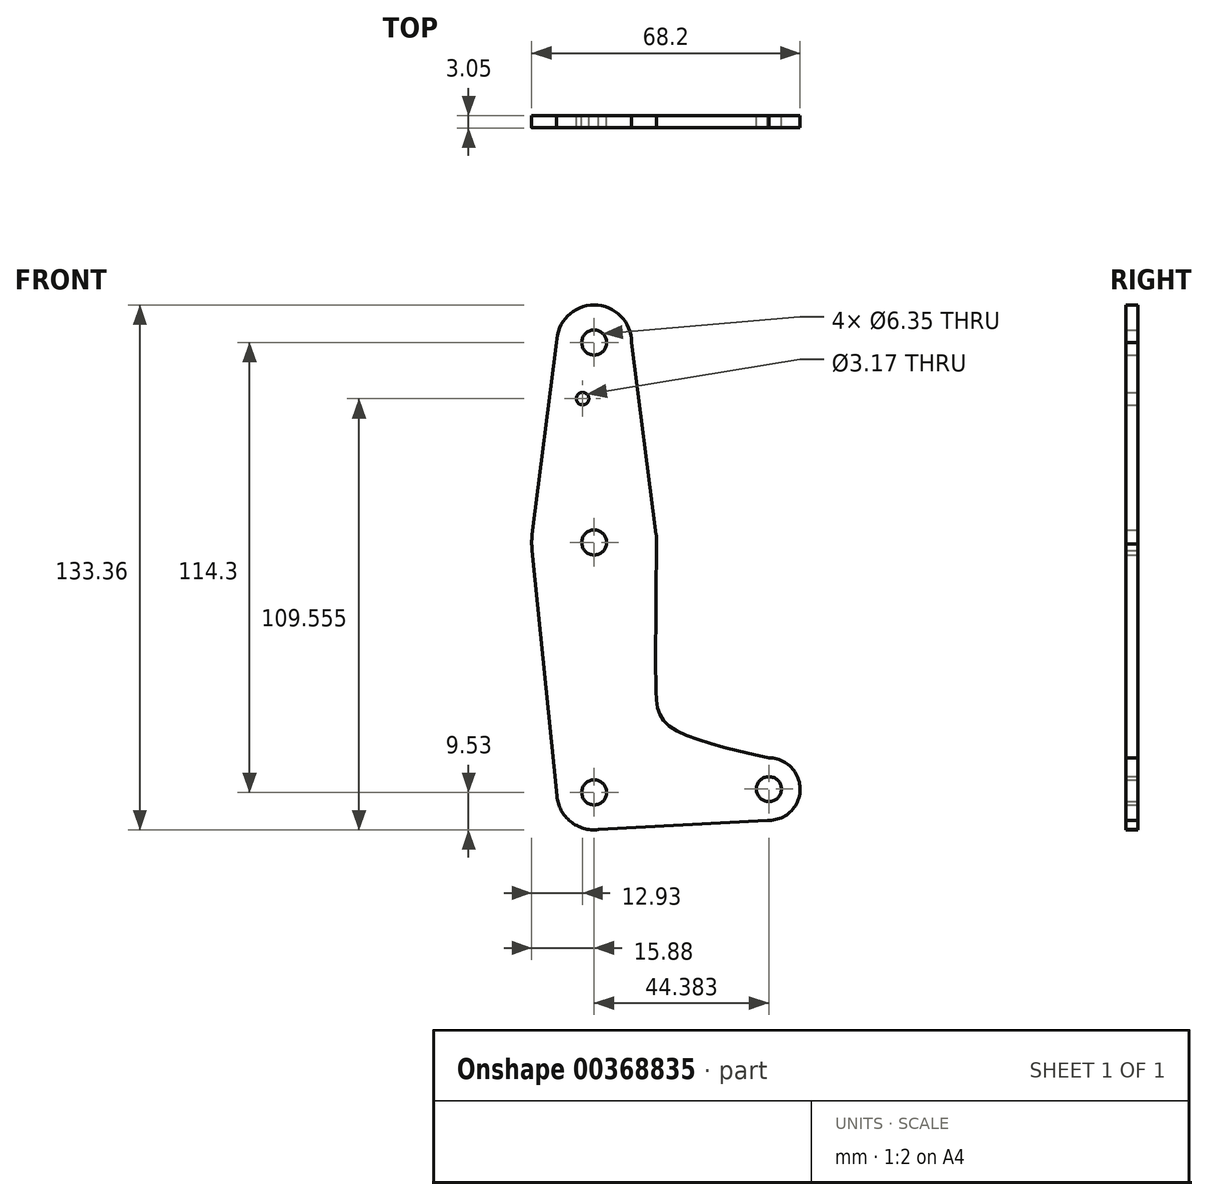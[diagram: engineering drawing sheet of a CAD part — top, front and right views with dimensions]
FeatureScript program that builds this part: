
annotation { "Feature Type Name" : "Feature", "Feature Type Description" : "" }
export const myFeature = defineFeature(function(context is Context, id is Id, definition is map)
    precondition{}
    {
        {
            var Q0;
            Q0=qCreatedBy(makeId("Front.planeOp"),FACE);
            var sketch = newSketch(context, id + "F0", { "sketchPlane" : qUnion([Q0])});
            skCircle(sketch, "E0", {"center": v(0, 0) * mm, "radius": 3.18 * mm});
            skCircle(sketch, "E1", {"center": v(0, 0) * mm, "radius": 15.88 * mm});
            skLineSegment(sketch, "E2", {"start": v(-63.05, 50.8) * mm, "end": v(-63.05, -63.5) * mm});
            skCircle(sketch, "E3", {"center": v(0, 50.8) * mm, "radius": 3.18 * mm});
            skCircle(sketch, "E4", {"center": v(0, 50.8) * mm, "radius": 9.53 * mm});
            skCircle(sketch, "E5", {"center": v(0, -63.5) * mm, "radius": 3.18 * mm});
            skCircle(sketch, "E6", {"center": v(0, -63.5) * mm, "radius": 9.53 * mm});
            skLineSegment(sketch, "E7", {"start": v(-9.52, 50.8) * mm, "end": v(-15.75, 2) * mm});
            skLineSegment(sketch, "E8", {"start": v(9.52, 50.8) * mm, "end": v(15.75, 2) * mm});
            skLineSegment(sketch, "E9", {"start": v(34.66, 36.53) * mm, "end": v(34.66, 0) * mm});
            skCircle(sketch, "E10", {"center": v(-2.95, 36.53) * mm, "radius": 1.59 * mm});
            skLineSegment(sketch, "E11", {"start": v(-15.75, -2) * mm, "end": v(-9.48, -64.45) * mm});
            skCircle(sketch, "E12", {"center": v(44.38, -62.68) * mm, "radius": 3.18 * mm});
            skCircle(sketch, "E13", {"center": v(44.38, -62.68) * mm, "radius": 7.94 * mm});
            skLineSegment(sketch, "E14", {"start": v(-39.82, -63.5) * mm, "end": v(-39.82, 0) * mm});
            skLineSegment(sketch, "E15", {"start": v(0, -73.03) * mm, "end": v(44.38, -70.58) * mm});
            skFitSpline(sketch, "E16", {"points": [v(15.88, 0) * mm, v(15.67, -36.87) * mm, v(18.44, -46.09) * mm, v(44.38, -54.74) * mm], "startDerivative": vector(-1.31, -101.52) * mm, "endDerivative": vector(89.73, -20.14) * mm});
            skSolve(sketch);
        }
        {
            var Q0;
            Q0 = qSketchRegion(id + "F0", true);
            extrude(context, id + "F1", {"entities" : qUnion([Q0]), "depth" : 3.05 * mm});
        }
    });
